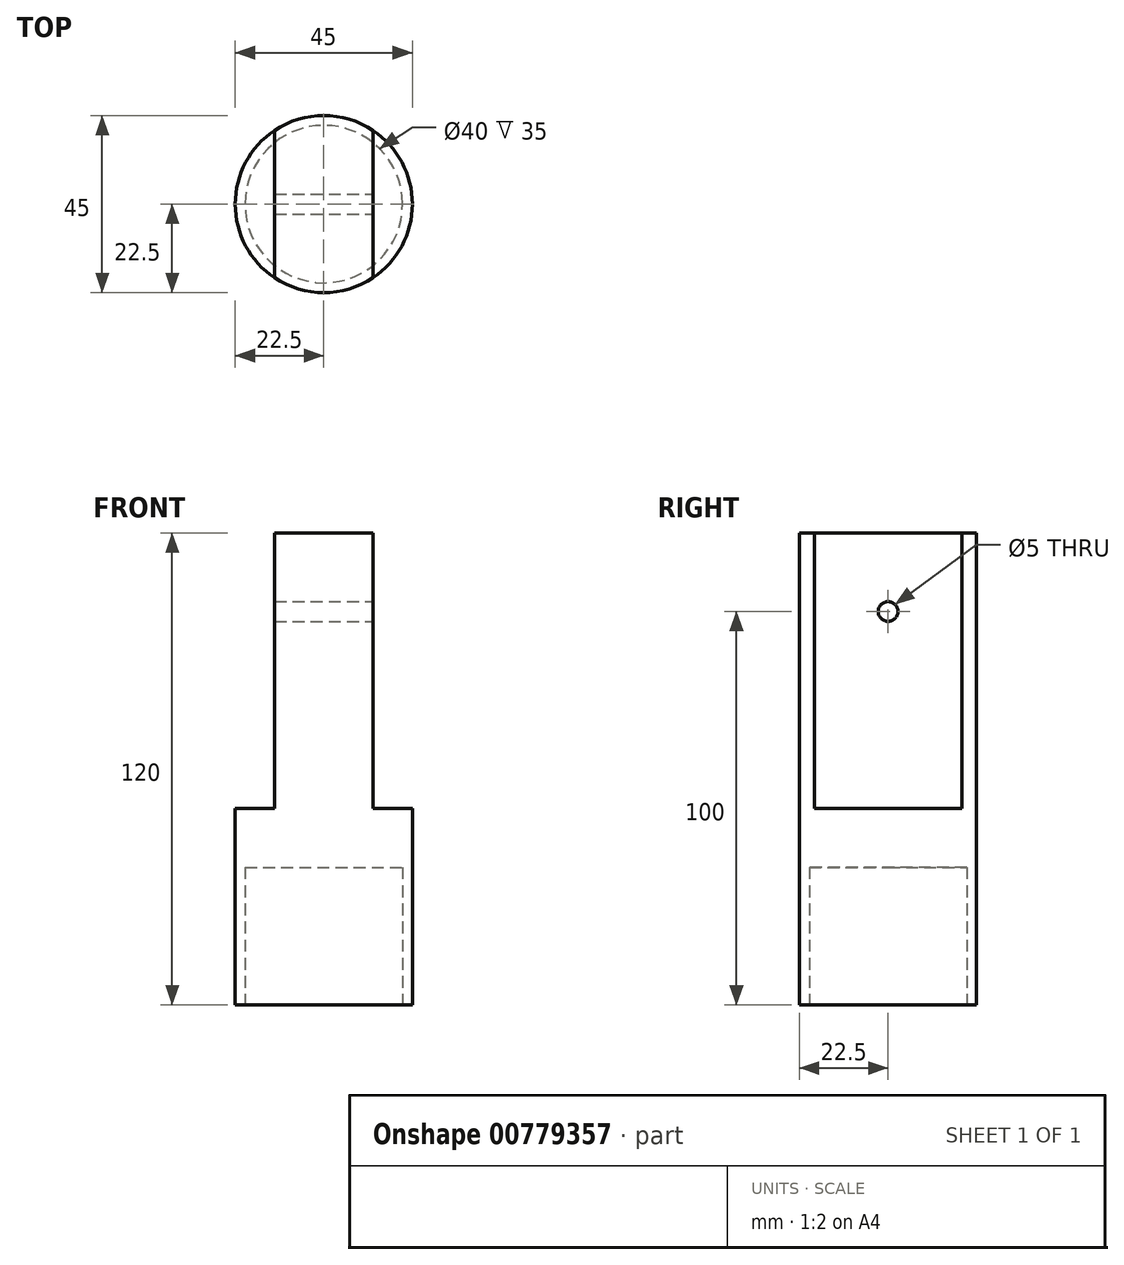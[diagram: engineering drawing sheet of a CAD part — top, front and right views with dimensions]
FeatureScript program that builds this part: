
annotation { "Feature Type Name" : "Feature", "Feature Type Description" : "" }
export const myFeature = defineFeature(function(context is Context, id is Id, definition is map)
    precondition{}
    {
        {
            var Q0;
            Q0=qCreatedBy(makeId("Top.planeOp"),FACE);
            var sketch = newSketch(context, id + "F0", { "sketchPlane" : qUnion([Q0])});
            skCircle(sketch, "E0", {"center": v(0, 0) * mm, "radius": 22.5 * mm});
            skSolve(sketch);
        }
        {
            var Q0;
            Q0=makeQuery(id+"F0.imprint","IMPRINT",FACE,{"disambiguationData":[TD([[makeQuery(id+"F0.imprint","IMPRINT",EDGE,{"derivedFrom":sQuery(id+"F0.wireOp",EDGE,"E0")}),1.0]])]});
            extrude(context, id + "F1", {"entities" : qUnion([Q0]), "depth" : 120 * mm, "offsetDistance" : 25 * mm});
        }
        {
            var Q0;
            Q0=makeQuery(id+"F1.opExtrude","CAP_FACE",FACE,{"disambiguationData":[OSD([sQuery(id+"F0.wireOp",EDGE,"E0")])],"isStart":false});
            var sketch = newSketch(context, id + "F2", { "sketchPlane" : qUnion([Q0])});
            skLineSegment(sketch, "E1", {"start": v(-12.5, 18.7) * mm, "end": v(-12.5, -18.7) * mm});
            skLineSegment(sketch, "E2", {"start": v(12.5, 18.7) * mm, "end": v(12.5, -18.7) * mm});
            skSolve(sketch);
        }
        {
            var Q0;
            {var subQ0=sQuery(id+"F2.wireOp",EDGE,"E1");Q0=makeQuery(id+"F2.imprint","IMPRINT",FACE,{"disambiguationData":[TD([[makeQuery(id+"F2.imprint","IMPRINT",EDGE,{"derivedFrom":subQ0}),-1.0]])]});}
            var Q1;
            {var subQ0=sQuery(id+"F2.wireOp",EDGE,"E2");Q1=makeQuery(id+"F2.imprint","IMPRINT",FACE,{"disambiguationData":[TD([[makeQuery(id+"F2.imprint","IMPRINT",EDGE,{"derivedFrom":subQ0}),1.0]])]});}
            extrude(context, id + "F3", {"entities" : qUnion([Q0, Q1]), "operationType" : NewBodyOperationType.REMOVE, "oppositeDirection" : true, "depth" : 70 * mm, "offsetDistance" : 25 * mm});
        }
        {
            var Q0;
            Q0=makeQuery(id+"F1.opExtrude","CAP_FACE",FACE,{"disambiguationData":[OSD([sQuery(id+"F0.wireOp",EDGE,"E0")])],"isStart":true});
            var sketch = newSketch(context, id + "F4", { "sketchPlane" : qUnion([Q0])});
            skCircle(sketch, "E3", {"center": v(0, 0) * mm, "radius": 20 * mm});
            skSolve(sketch);
        }
        {
            var Q0;
            Q0=makeQuery(id+"F4.imprint","IMPRINT",FACE,{"disambiguationData":[TD([[makeQuery(id+"F4.imprint","IMPRINT",EDGE,{"derivedFrom":sQuery(id+"F4.wireOp",EDGE,"E3")}),1.0]])]});
            extrude(context, id + "F5", {"entities" : qUnion([Q0]), "operationType" : NewBodyOperationType.REMOVE, "oppositeDirection" : true, "depth" : 35 * mm, "offsetDistance" : 25 * mm});
        }
        {
            var Q0;
            Q0=qCreatedBy(makeId("Right.planeOp"),FACE);
            cPlane(context, id + "F6", {"entities" : qUnion([Q0]), "cplaneType" : CPlaneType.OFFSET, "offset" : 22.5 * mm, "width" : 150 * mm, "height" : 150 * mm});
        }
        {
            var Q0;
            Q0=qCreatedBy(id+"F6.planeOp",FACE);
            var sketch = newSketch(context, id + "F7", { "sketchPlane" : qUnion([Q0])});
            skLineSegment(sketch, "E4", {"start": v(-18.7, 100) * mm, "end": v(18.7, 100) * mm});
            skPoint(sketch, "E5", {"position": v(0, 100) * mm});
            skSolve(sketch);
        }
        {
            var Q0;
            Q0=sQuery(id+"F7.wireOp",VERTEX,"E5");
            var Q1;
            Q1=makeQuery(id+"F1.opExtrude","SWEPT_BODY",BODY,{"disambiguationData":[OSD([sQuery(id+"F0.wireOp",EDGE,"E0")])]});
            hole(context, id + "F8", {"style" : HoleStyle.SIMPLE, "endStyle" : HoleEndStyle.THROUGH, "holeDiameter" : 5 * mm, "majorDiameter" : 5 * mm, "isTappedThrough" : true, "tappedDepth" : 12 * mm, "tapClearance" : 3, "locations" : qUnion([Q0]), "scope" : qUnion([Q1])});
        }
    });
